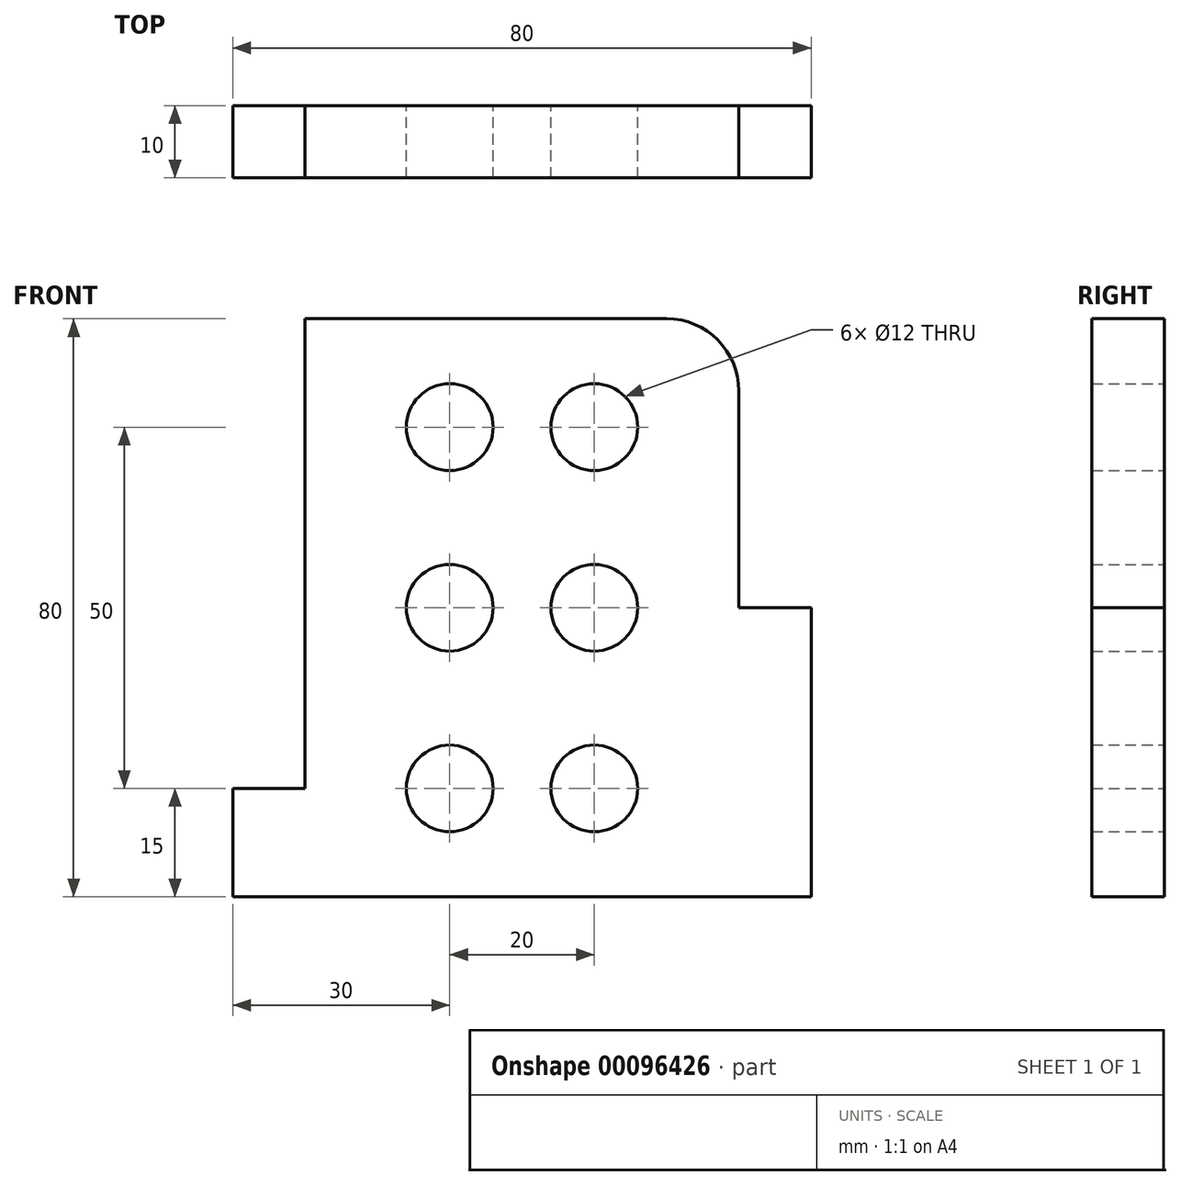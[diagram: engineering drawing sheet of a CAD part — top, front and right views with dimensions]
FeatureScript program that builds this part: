
annotation { "Feature Type Name" : "Feature", "Feature Type Description" : "" }
export const myFeature = defineFeature(function(context is Context, id is Id, definition is map)
    precondition{}
    {
        {
            var Q0;
            Q0=qCreatedBy(makeId("Front.planeOp"),FACE);
            var sketch = newSketch(context, id + "F0", { "sketchPlane" : qUnion([Q0])});
            skLineSegment(sketch, "E0.bottom", {"start": v(0, 0) * mm, "end": v(80, 0) * mm, "construction": true});
            skLineSegment(sketch, "E0.top", {"start": v(0, 80) * mm, "end": v(80, 80) * mm, "construction": true});
            skLineSegment(sketch, "E0.left", {"start": v(0, 0) * mm, "end": v(0, 80) * mm, "construction": true});
            skLineSegment(sketch, "E0.right", {"start": v(80, 0) * mm, "end": v(80, 80) * mm, "construction": true});
            skLineSegment(sketch, "E1", {"start": v(0, 0) * mm, "end": v(80, 0) * mm});
            skLineSegment(sketch, "E2", {"start": v(80, 0) * mm, "end": v(80, 40) * mm});
            skLineSegment(sketch, "E3", {"start": v(80, 40) * mm, "end": v(70, 40) * mm});
            skLineSegment(sketch, "E4", {"start": v(70, 40) * mm, "end": v(70, 70) * mm});
            skLineSegment(sketch, "E5", {"start": v(60, 80) * mm, "end": v(0, 80) * mm});
            skLineSegment(sketch, "E6", {"start": v(0, 0) * mm, "end": v(0, 15) * mm});
            skLineSegment(sketch, "E7", {"start": v(10, 15) * mm, "end": v(0, 15) * mm});
            skLineSegment(sketch, "E8", {"start": v(10, 15) * mm, "end": v(10, 80) * mm});
            skPoint(sketch, "E9.visualSharp", {"position": v(70, 80) * mm});
            skArc(sketch, "E9.filletArc", {"start": v(70, 70) * mm, "mid": v(67.07, 77.07) * mm, "end": v(60, 80) * mm});
            skCircle(sketch, "E10", {"center": v(50, 65) * mm, "radius": 6 * mm});
            skCircle(sketch, "E11", {"center": v(50, 40) * mm, "radius": 6 * mm});
            skCircle(sketch, "E12", {"center": v(50, 15) * mm, "radius": 6 * mm});
            skCircle(sketch, "E13", {"center": v(30, 15) * mm, "radius": 6 * mm});
            skCircle(sketch, "E14", {"center": v(30, 40) * mm, "radius": 6 * mm});
            skCircle(sketch, "E15", {"center": v(30, 65) * mm, "radius": 6 * mm});
            skSolve(sketch);
        }
        {
            var Q0;
            Q0 = qSketchRegion(id + "F0", true);
            extrude(context, id + "F1", {"entities" : qUnion([Q0]), "endBound" : BoundingType.SYMMETRIC, "depth" : 10 * mm});
        }
    });
